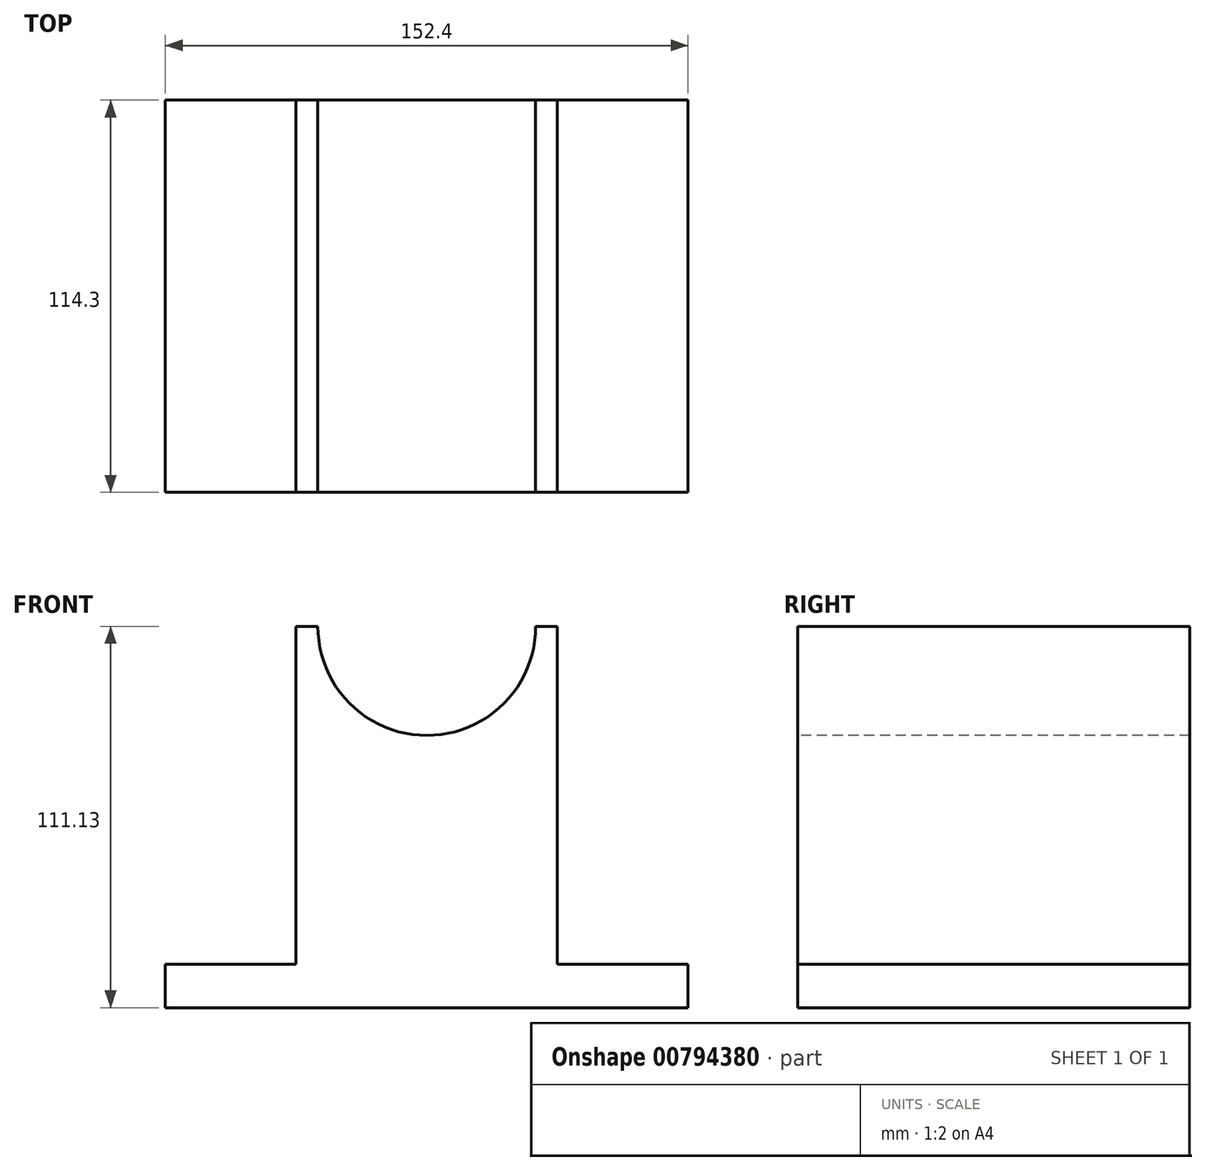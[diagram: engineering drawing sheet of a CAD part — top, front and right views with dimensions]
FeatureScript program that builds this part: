
annotation { "Feature Type Name" : "Feature", "Feature Type Description" : "" }
export const myFeature = defineFeature(function(context is Context, id is Id, definition is map)
    precondition{}
    {
        {
            var Q0;
            Q0=qCreatedBy(makeId("Front.planeOp"),FACE);
            var sketch = newSketch(context, id + "F0", { "sketchPlane" : qUnion([Q0])});
            skLineSegment(sketch, "E0", {"start": v(0, 0) * mm, "end": v(152.4, 0) * mm});
            skLineSegment(sketch, "E1", {"start": v(152.4, 0) * mm, "end": v(152.4, 111.13) * mm});
            skLineSegment(sketch, "E2", {"start": v(152.4, 111.13) * mm, "end": v(0, 111.13) * mm});
            skLineSegment(sketch, "E3", {"start": v(0, 111.13) * mm, "end": v(0, 0) * mm});
            skSolve(sketch);
        }
        {
            var Q0;
            Q0=makeQuery(id+"F0.imprint","IMPRINT",FACE,{"disambiguationData":[TD([[makeQuery(id+"F0.imprint","IMPRINT",EDGE,{"derivedFrom":sQuery(id+"F0.wireOp",EDGE,"E0")}),1.0]])]});
            extrude(context, id + "F1", {"entities" : qUnion([Q0]), "depth" : 114.3 * mm, "offsetDistance" : 25.4 * mm});
        }
        {
            var Q0;
            Q0=makeQuery(id+"F1.opExtrude","CAP_FACE",FACE,{"disambiguationData":[OSD([sQuery(id+"F0.wireOp",EDGE,"E0"),sQuery(id+"F0.wireOp",EDGE,"E1"),sQuery(id+"F0.wireOp",EDGE,"E2"),sQuery(id+"F0.wireOp",EDGE,"E3")])],"isStart":false});
            var sketch = newSketch(context, id + "F2", { "sketchPlane" : qUnion([Q0])});
            skLineSegment(sketch, "E4", {"start": v(0, 0) * mm, "end": v(0, 12.7) * mm});
            skLineSegment(sketch, "E5", {"start": v(0, 12.7) * mm, "end": v(38.1, 12.7) * mm});
            skLineSegment(sketch, "E6", {"start": v(38.1, 12.7) * mm, "end": v(38.1, 111.13) * mm});
            skLineSegment(sketch, "E7", {"start": v(152.4, 0) * mm, "end": v(152.4, 12.7) * mm});
            skLineSegment(sketch, "E8", {"start": v(152.4, 12.7) * mm, "end": v(114.3, 12.7) * mm});
            skLineSegment(sketch, "E9", {"start": v(38.1, 111.13) * mm, "end": v(114.3, 111.13) * mm});
            skLineSegment(sketch, "E10", {"start": v(114.3, 111.13) * mm, "end": v(114.3, 12.7) * mm});
            skSolve(sketch);
        }
        {
            var Q0;
            {var subQ0=sQuery(id+"F2.wireOp",EDGE,"E5");Q0=makeQuery(id+"F2.imprint","IMPRINT",FACE,{"disambiguationData":[TD([[makeQuery(id+"F2.imprint","IMPRINT",EDGE,{"derivedFrom":subQ0}),1.0]])]});}
            var Q1;
            {var subQ0=sQuery(id+"F2.wireOp",EDGE,"E8");Q1=makeQuery(id+"F2.imprint","IMPRINT",FACE,{"disambiguationData":[TD([[makeQuery(id+"F2.imprint","IMPRINT",EDGE,{"derivedFrom":subQ0}),-1.0]])]});}
            extrude(context, id + "F3", {"entities" : qUnion([Q0, Q1]), "operationType" : NewBodyOperationType.REMOVE, "oppositeDirection" : true, "depth" : 114.3 * mm, "offsetDistance" : 25.4 * mm});
        }
        {
            var Q0;
            Q0=makeQuery(id+"F1.opExtrude","CAP_FACE",FACE,{"disambiguationData":[OSD([sQuery(id+"F0.wireOp",EDGE,"E0"),sQuery(id+"F0.wireOp",EDGE,"E1"),sQuery(id+"F0.wireOp",EDGE,"E2"),sQuery(id+"F0.wireOp",EDGE,"E3")])],"isStart":false});
            var sketch = newSketch(context, id + "F4", { "sketchPlane" : qUnion([Q0])});
            skLineSegment(sketch, "E11", {"start": v(38.1, 111.13) * mm, "end": v(44.45, 111.13) * mm, "construction": true});
            skLineSegment(sketch, "E12", {"start": v(114.3, 111.13) * mm, "end": v(107.95, 111.13) * mm, "construction": true});
            skArc(sketch, "E13", {"start": v(44.45, 111.12) * mm, "mid": v(76.2, 79.33) * mm, "end": v(107.95, 111.13) * mm});
            skSolve(sketch);
        }
        {
            var Q0;
            {var subQ0=sQuery(id+"F4.wireOp",EDGE,"E13");Q0=makeQuery(id+"F4.imprint","IMPRINT",FACE,{"disambiguationData":[TD([[makeQuery(id+"F4.imprint","IMPRINT",EDGE,{"derivedFrom":subQ0}),1.0]])]});}
            extrude(context, id + "F5", {"entities" : qUnion([Q0]), "operationType" : NewBodyOperationType.REMOVE, "oppositeDirection" : true, "depth" : 114.3 * mm, "offsetDistance" : 25.4 * mm});
        }
    });
